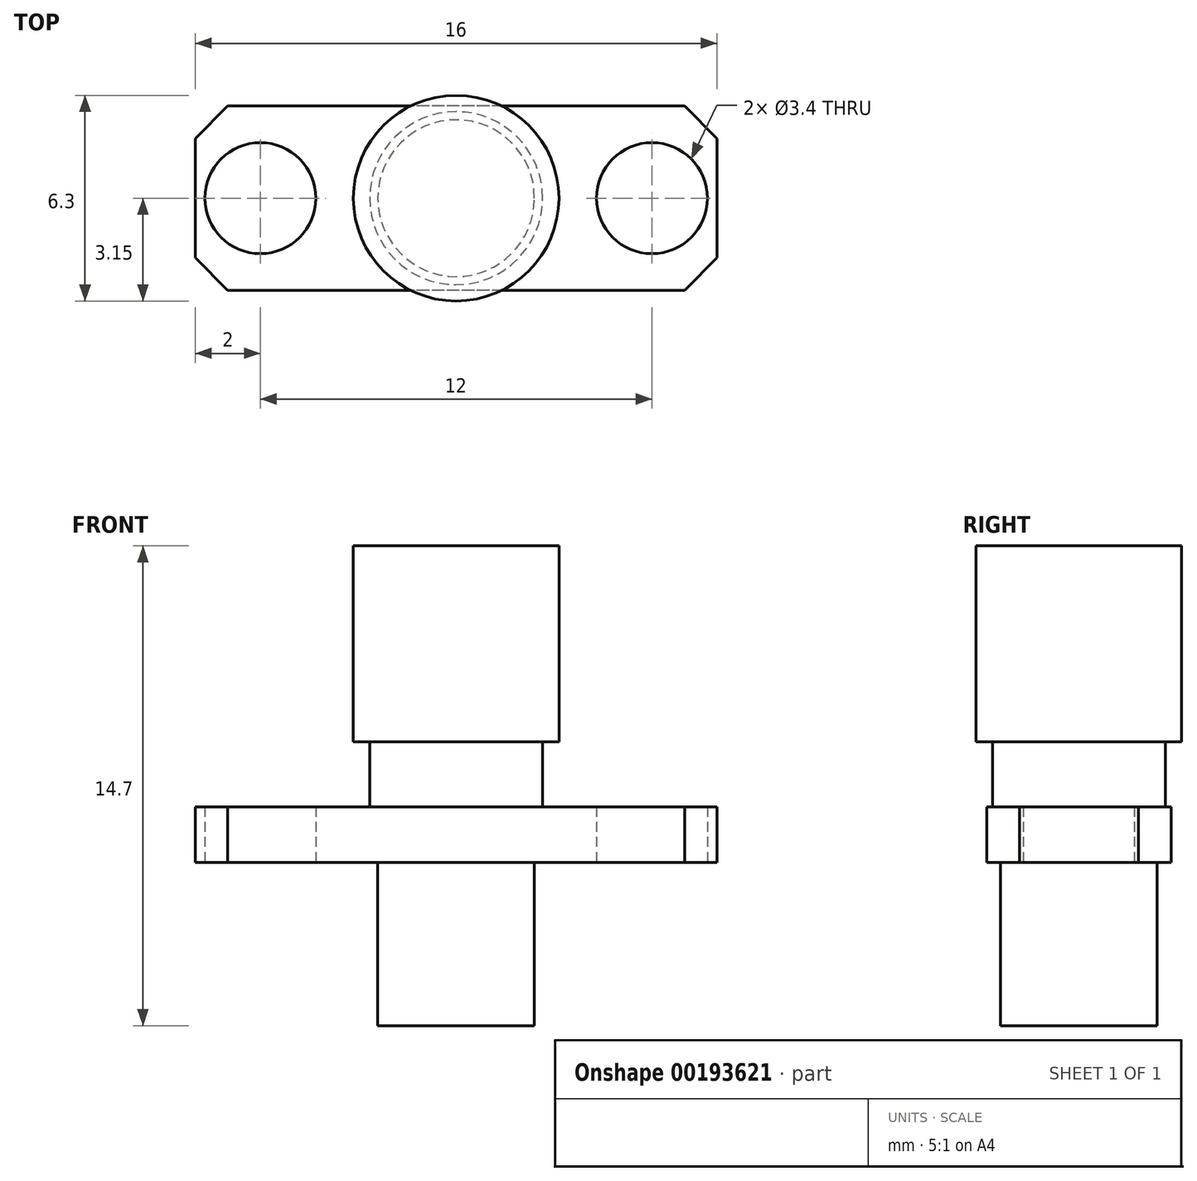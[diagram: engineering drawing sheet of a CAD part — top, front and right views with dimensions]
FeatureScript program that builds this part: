
annotation { "Feature Type Name" : "Feature", "Feature Type Description" : "" }
export const myFeature = defineFeature(function(context is Context, id is Id, definition is map)
    precondition{}
    {
        {
            var Q0;
            Q0=qCreatedBy(makeId("Top.planeOp"),FACE);
            var sketch = newSketch(context, id + "F0", { "sketchPlane" : qUnion([Q0])});
            skLineSegment(sketch, "E0.bottom", {"start": v(8, -2.82) * mm, "end": v(-8, -2.82) * mm});
            skLineSegment(sketch, "E0.top", {"start": v(8, 2.83) * mm, "end": v(-8, 2.83) * mm});
            skLineSegment(sketch, "E0.left", {"start": v(8, -2.82) * mm, "end": v(8, 2.83) * mm});
            skLineSegment(sketch, "E0.right", {"start": v(-8, -2.82) * mm, "end": v(-8, 2.82) * mm});
            skPoint(sketch, "E0.middle", {"position": v(0, 0) * mm});
            skCircle(sketch, "E1", {"center": v(0, 0) * mm, "radius": 3.15 * mm});
            skCircle(sketch, "E2", {"center": v(0, 0) * mm, "radius": 2.65 * mm});
            skCircle(sketch, "E3", {"center": v(-6, 0) * mm, "radius": 1.7 * mm});
            skCircle(sketch, "E4", {"center": v(6, 0) * mm, "radius": 1.7 * mm});
            skLineSegment(sketch, "E5", {"start": v(-6, 0) * mm, "end": v(6, 0) * mm, "construction": true});
            skSolve(sketch);
        }
        {
            var Q0;
            {var subQ5=sQuery(id+"F0.wireOp",EDGE,"E0.left");Q0=makeQuery(id+"F0.imprint","IMPRINT",FACE,{"disambiguationData":[TD([[makeQuery(id+"F0.imprint","IMPRINT",EDGE,{"derivedFrom":subQ5}),1.0]])]});}
            var Q1;
            {var subQ5=sQuery(id+"F0.wireOp",EDGE,"E0.right");Q1=makeQuery(id+"F0.imprint","IMPRINT",FACE,{"disambiguationData":[TD([[makeQuery(id+"F0.imprint","IMPRINT",EDGE,{"derivedFrom":subQ5}),-1.0]])]});}
            var Q2;
            Q2=makeQuery(id+"F0.imprint","IMPRINT",FACE,{"disambiguationData":[TD([[makeQuery(id+"F0.imprint","IMPRINT",EDGE,{"derivedFrom":sQuery(id+"F0.wireOp",EDGE,"E2")}),-1.0]])]});
            var Q3;
            Q3=makeQuery(id+"F0.imprint","IMPRINT",FACE,{"disambiguationData":[TD([[makeQuery(id+"F0.imprint","IMPRINT",EDGE,{"derivedFrom":sQuery(id+"F0.wireOp",EDGE,"E2")}),1.0]])]});
            extrude(context, id + "F1", {"entities" : qUnion([Q0, Q1, Q2, Q3]), "depth" : 1.7 * mm, "offsetDistance" : 25 * mm});
        }
        {
            var Q0;
            Q0=makeQuery(id+"F1.opExtrude","CAP_FACE",FACE,{"disambiguationData":[OSD([sQuery(id+"F0.wireOp",EDGE,"E0.bottom"),sQuery(id+"F0.wireOp",EDGE,"E0.top"),sQuery(id+"F0.wireOp",EDGE,"E0.left"),sQuery(id+"F0.wireOp",EDGE,"E0.right"),sQuery(id+"F0.wireOp",EDGE,"E3"),sQuery(id+"F0.wireOp",EDGE,"E4")])],"isStart":false});
            var sketch = newSketch(context, id + "F2", { "sketchPlane" : qUnion([Q0])});
            skCircle(sketch, "E6.0", {"center": v(0, 0) * mm, "radius": 2.65 * mm});
            skSolve(sketch);
        }
        {
            var Q0;
            Q0=makeQuery(id+"F2.imprint","IMPRINT",FACE,{"disambiguationData":[TD([[makeQuery(id+"F2.imprint","IMPRINT",EDGE,{"derivedFrom":sQuery(id+"F2.wireOp",EDGE,"E6.0")}),1.0]])]});
            extrude(context, id + "F3", {"entities" : qUnion([Q0]), "operationType" : NewBodyOperationType.ADD, "depth" : 2 * mm, "offsetDistance" : 25 * mm});
        }
        {
            var Q0;
            Q0=makeQuery(id+"F3.opExtrude","CAP_FACE",FACE,{"disambiguationData":[OSD([sQuery(id+"F2.wireOp",EDGE,"E6.0")])],"isStart":false});
            var sketch = newSketch(context, id + "F4", { "sketchPlane" : qUnion([Q0])});
            skCircle(sketch, "E7.0", {"center": v(0, 0) * mm, "radius": 3.15 * mm});
            skSolve(sketch);
        }
        {
            var Q0;
            Q0 = qSketchRegion(id + "F4", true);
            extrude(context, id + "F5", {"entities" : qUnion([Q0]), "operationType" : NewBodyOperationType.ADD, "depth" : (8 - 2) * mm, "offsetDistance" : 25 * mm});
        }
        {
            var Q0;
            Q0=makeQuery(id+"F1.opExtrude","SWEPT_EDGE",EDGE,{"disambiguationData":[OSD([sQuery(id+"F0.wireOp",EDGE,"E0.bottom"),sQuery(id+"F0.wireOp",EDGE,"E0.right")])]});
            var Q1;
            Q1=makeQuery(id+"F1.opExtrude","SWEPT_EDGE",EDGE,{"disambiguationData":[OSD([sQuery(id+"F0.wireOp",EDGE,"E0.top"),sQuery(id+"F0.wireOp",EDGE,"E0.right")])]});
            var Q2;
            Q2=makeQuery(id+"F1.opExtrude","SWEPT_EDGE",EDGE,{"disambiguationData":[OSD([sQuery(id+"F0.wireOp",EDGE,"E0.bottom"),sQuery(id+"F0.wireOp",EDGE,"E0.left")])]});
            var Q3;
            Q3=makeQuery(id+"F1.opExtrude","SWEPT_EDGE",EDGE,{"disambiguationData":[OSD([sQuery(id+"F0.wireOp",EDGE,"E0.top"),sQuery(id+"F0.wireOp",EDGE,"E0.left")])]});
            chamfer(context, id + "F6", {"entities" : qUnion([Q0, Q1, Q2, Q3]), "width" : 1 * mm, "tangentPropagation" : true});
        }
        {
            var Q0;
            Q0=makeQuery(id+"F0.imprint","IMPRINT",FACE,{"disambiguationData":[TD([[makeQuery(id+"F0.imprint","IMPRINT",EDGE,{"derivedFrom":sQuery(id+"F0.wireOp",EDGE,"E2")}),1.0]])]});
            var sketch = newSketch(context, id + "F7", { "sketchPlane" : qUnion([Q0])});
            skCircle(sketch, "E8", {"center": v(0, 0) * mm, "radius": 2.4 * mm});
            skSolve(sketch);
        }
        {
            var Q0;
            Q0 = qSketchRegion(id + "F7", true);
            var Q1;
            Q1=sQuery(id+"F7.wireOp",EDGE,"E8");
            extrude(context, id + "F8", {"entities" : qUnion([Q0]), "operationType" : NewBodyOperationType.ADD, "surfaceEntities" : qUnion([Q1]), "oppositeDirection" : true, "depth" : 5 * mm, "offsetDistance" : 25 * mm});
        }
    });
